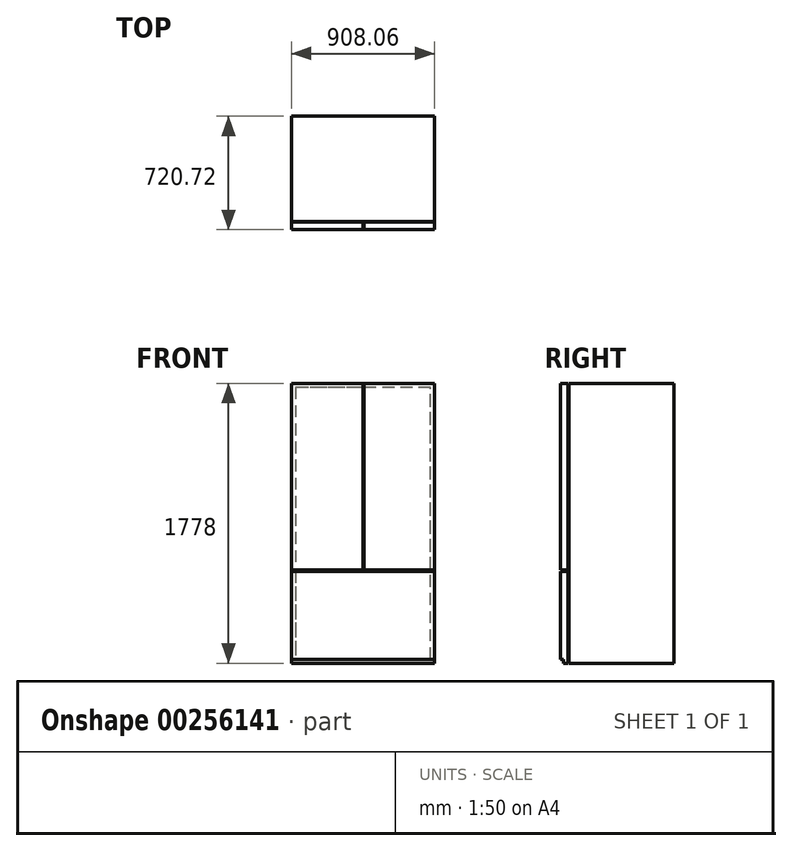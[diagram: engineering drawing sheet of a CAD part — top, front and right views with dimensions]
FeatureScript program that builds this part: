
annotation { "Feature Type Name" : "Feature", "Feature Type Description" : "" }
export const myFeature = defineFeature(function(context is Context, id is Id, definition is map)
    precondition{}
    {
        {
            var Q0;
            Q0=qCreatedBy(makeId("Right.planeOp"),FACE);
            var sketch = newSketch(context, id + "F0", { "sketchPlane" : qUnion([Q0])});
            skLineSegment(sketch, "E0", {"start": v(0, 0) * mm, "end": v(0, 1778) * mm});
            skLineSegment(sketch, "E1", {"start": v(0, 0) * mm, "end": v(-720.73, 0) * mm});
            skLineSegment(sketch, "E2", {"start": v(-720.73, 0) * mm, "end": v(-720.73, 1778) * mm});
            skLineSegment(sketch, "E3", {"start": v(-720.73, 1778) * mm, "end": v(0, 1778) * mm});
            skSolve(sketch);
        }
        {
            var Q0;
            Q0=makeQuery(id+"F0.imprint","IMPRINT",FACE,{"disambiguationData":[TD([[makeQuery(id+"F0.imprint","IMPRINT",EDGE,{"derivedFrom":sQuery(id+"F0.wireOp",EDGE,"E0")}),1.0]])]});
            extrude(context, id + "F1", {"entities" : qUnion([Q0]), "endBound" : BoundingType.SYMMETRIC, "depth" : 908.05 * mm});
        }
        {
            var Q0;
            Q0=makeQuery(id+"F1.opExtrude","SWEPT_FACE",FACE,{"disambiguationData":[OSD([sQuery(id+"F0.wireOp",EDGE,"E2")])]});
            cPlane(context, id + "F2", {"entities" : qUnion([Q0]), "cplaneType" : CPlaneType.OFFSET, "offset" : 50.8 * mm, "oppositeDirection" : true, "width" : 152.4 * mm, "height" : 152.4 * mm});
        }
        {
            var Q0;
            Q0=qCreatedBy(id+"F2.planeOp",FACE);
            var sketch = newSketch(context, id + "F3", { "sketchPlane" : qUnion([Q0])});
            skLineSegment(sketch, "E4.0", {"start": v(-428.63, 1752.6) * mm, "end": v(-428.63, 25.4) * mm});
            skLineSegment(sketch, "E4.1", {"start": v(428.63, 1752.6) * mm, "end": v(-428.63, 1752.6) * mm});
            skLineSegment(sketch, "E4.2", {"start": v(428.63, 25.4) * mm, "end": v(428.63, 1752.6) * mm});
            skLineSegment(sketch, "E4.3", {"start": v(-428.63, 25.4) * mm, "end": v(428.63, 25.4) * mm});
            skLineSegment(sketch, "E5.0.0", {"start": v(-454.03, 1778) * mm, "end": v(-454.03, 0) * mm});
            skLineSegment(sketch, "E5.0.1", {"start": v(-454.03, 0) * mm, "end": v(454.03, 0) * mm});
            skLineSegment(sketch, "E5.0.2", {"start": v(454.03, 0) * mm, "end": v(454.03, 1778) * mm});
            skLineSegment(sketch, "E5.0.3", {"start": v(454.03, 1778) * mm, "end": v(-454.03, 1778) * mm});
            skSolve(sketch);
        }
        {
            var Q0;
            Q0 = qSketchRegion(id + "F3", true);
            extrude(context, id + "F4", {"entities" : qUnion([Q0]), "operationType" : NewBodyOperationType.REMOVE, "endBound" : BoundingType.SYMMETRIC, "depth" : 3.8 * mm});
        }
        {
            var Q0;
            Q0=makeQuery(id+"F1.opExtrude","SWEPT_FACE",FACE,{"disambiguationData":[OSD([sQuery(id+"F0.wireOp",EDGE,"E2")])]});
            var sketch = newSketch(context, id + "F5", { "sketchPlane" : qUnion([Q0])});
            skLineSegment(sketch, "E6.bottom", {"start": v(454.03, 0) * mm, "end": v(-454.03, 0) * mm});
            skLineSegment(sketch, "E6.top", {"start": v(454.03, 25.4) * mm, "end": v(-454.03, 25.4) * mm});
            skLineSegment(sketch, "E6.left", {"start": v(454.03, 0) * mm, "end": v(454.03, 25.4) * mm});
            skLineSegment(sketch, "E6.right", {"start": v(-454.03, 0) * mm, "end": v(-454.03, 25.4) * mm});
            skSolve(sketch);
        }
        {
            var Q0;
            Q0=makeQuery(id+"F1.opExtrude","SWEPT_FACE",FACE,{"disambiguationData":[OSD([sQuery(id+"F0.wireOp",EDGE,"E2")])]});
            var sketch = newSketch(context, id + "F6", { "sketchPlane" : qUnion([Q0])});
            skLineSegment(sketch, "E7.bottom", {"start": v(0, 1778) * mm, "end": v(7.62, 1778) * mm});
            skLineSegment(sketch, "E7.left", {"start": v(0, 1778) * mm, "end": v(0, 591.82) * mm});
            skLineSegment(sketch, "E7.right", {"start": v(7.62, 1778) * mm, "end": v(7.62, 591.82) * mm});
            skLineSegment(sketch, "E8.bottom", {"start": v(-480.07, 591.82) * mm, "end": v(0, 591.82) * mm});
            skLineSegment(sketch, "E8.top", {"start": v(-480.07, 584.2) * mm, "end": v(491.16, 584.2) * mm});
            skLineSegment(sketch, "E8.left", {"start": v(-480.07, 591.82) * mm, "end": v(-480.07, 584.2) * mm});
            skLineSegment(sketch, "E8.right", {"start": v(491.16, 591.82) * mm, "end": v(491.16, 584.2) * mm});
            skLineSegment(sketch, "E9.trimOffspring", {"start": v(7.62, 591.82) * mm, "end": v(491.16, 591.82) * mm});
            skSolve(sketch);
        }
        {
            var Q0;
            Q0 = qSketchRegion(id + "F6", true);
            extrude(context, id + "F7", {"entities" : qUnion([Q0]), "operationType" : NewBodyOperationType.REMOVE, "oppositeDirection" : true, "depth" : 50.8 * mm});
        }
        {
            var Q0;
            Q0 = qSketchRegion(id + "F5", true);
            extrude(context, id + "F8", {"entities" : qUnion([Q0]), "operationType" : NewBodyOperationType.REMOVE, "oppositeDirection" : true, "depth" : 19.05 * mm});
        }
    });
